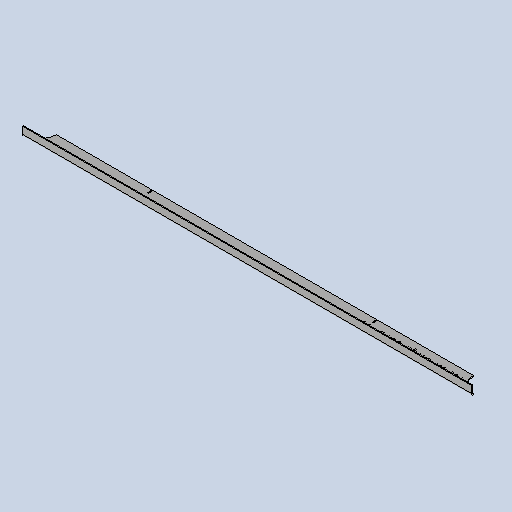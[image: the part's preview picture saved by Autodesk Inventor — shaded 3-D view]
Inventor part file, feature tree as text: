
AUTODESK INVENTOR PART (.ipt)
format: ipt  version: 2025 (Build 290162010, 162A)  size: 299,520 bytes
history: native  units: mm
features: other x5, sheet_metal_op x4, sketch x4, extrude x1
ambient origin geometry x8: Origin, YZ Plane, XZ Plane, XY Plane, X Axis, Y Axis, Z Axis, Center Point
bodies: Solid1 (feature_tree)
feature tree (14):
  sheet_metal_op  "Face1"
  sheet_metal_op  "Flange1"
  extrude  "Extrusion1"  Depth=39.0mm
  other  "Mark2"
  other  "A-Side Definition"
  sketch  "Sketch1"  dims[d0=980.0mm d1=39.0mm]
  other  "Plate1"
  sketch  "Sketch2"  dims[d2=2.0mm]
  other  "Plate2"
  sheet_metal_op  "Bend1"
  sheet_metal_op  "Corner1"
  sketch  "Sketch5"  dims[d3=2.0mm]
  sketch  "Sketch9"  dims[d4=1.0mm d5=4.0mm d6=2.75mm d7=20.0mm d8=90.0deg d9=2.75mm d10=8.0mm d11=2.0mm d12=2.75mm d15=0.0mm d16=0.0mm d40=200.0mm d41=12.0mm d45=70.0mm d48=2.1mm d49=490.0mm d51=29.0mm d52=10.0mm]
  other  "Definition1"
